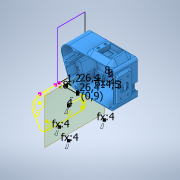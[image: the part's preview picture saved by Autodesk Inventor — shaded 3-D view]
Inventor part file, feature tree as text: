
AUTODESK INVENTOR PART (.ipt)
format: ipt  version: 2021.1 (Build 251245010, 245A)  size: 2,009,600 bytes
history: mixed  units: in
note: dims shown in document units (in); Inventor stores cm internally (conversion verified against a paired STEP export)
features: extrude x25, sketch x22, move_body x9, direct_edit x7, projected_geometry x7, chamfer x6, other x4, revolve x4, fillet x1, plane x1, imported_body x1
ambient origin geometry x8: Origin, YZ Plane, XZ Plane, XY Plane, X Axis, Y Axis, Z Axis, Center Point
bodies: Solid1 (imported_parasolid), Volumenkörper268 (imported_parasolid), Body1 (imported_parasolid)
feature tree (87):
  sketch  "Skizze1"  dims[d0=0.1575in d1=0.1575in]
  extrude  "Extrusion2"  Depth=0.1575in
  extrude  "Extrusion1"  Depth=0.1575in
  sketch  "Skizze3"  dims[d2=0.1575in d3=0.1575in]
  extrude  "Extrusion3"  Depth=0.252in TaperAngle=0.0deg
  extrude  "Extrusion4"  Depth=0.2756in TaperAngle=0.0deg
  extrude  "Extrusion5"  Depth=0.1575in
  extrude  "Extrusion6"  Depth=0.1575in
  direct_edit  "Direktbearbeitung2"
  extrude  "Extrusion8"  Depth=0.315in
  direct_edit  "Direktbearbeitung3"
  extrude  "Extrusion10"  Depth=0.1969in TaperAngle=0.0deg
  extrude  "Extrusion11"  TaperAngle=135.0deg  [1 undecoded]
  sketch  "Skizze16"  dims[d19=45.0deg d20=0.1969in d21=0.5906in d22=0.0in d23=0.0in]
  direct_edit  "Direktbearbeitung4"
  extrude  "Extrusion19"  TaperAngle=0.0deg  [1 undecoded]
  direct_edit  "Direktbearbeitung6"
  direct_edit  "Direktbearbeitung7"
  chamfer  "Fase2"  Distance=0.0157in
  extrude  "Extrusion26"  TaperAngle=135.0deg  [1 undecoded]
  chamfer  "Fase4"  Distance=0.3937in
  sketch  "Skizze29"  dims[d32=0.3937in d33=0.2362in d34=0.0in d35=0.0in d36=0.0in d37=0.0in d38=-0.0394in d39=0.0157in d40=0.0in]
  extrude  "Extrusion30"  TaperAngle=0.0deg  [1 undecoded]
  extrude  "Extrusion35"  Depth=1.0394in
  other  "Flächenverjüngung3"
  extrude  "Extrusion36"  Depth=0.0472in
  revolve  "Umdrehung1"
  sketch  "Skizze36"  dims[d45=0.3937in d46=0.0in d69=0.0in d70=0.0in d71=-0.2756in]
  fillet  "Rundung3"  Radius=0.315in
  extrude  "Extrusion37"  Depth=0.1181in TaperAngle=0.0deg
  chamfer  "Fase5"  [1 undecoded]
  plane  "Arbeitsebene2"
  extrude  "Extrusion38"  Depth=0.0197in
  extrude  "Extrusion39"  Depth=0.0197in
  extrude  "Extrusion40"  Depth=0.0197in TaperAngle=45.0deg
  chamfer  "Fase6"  Distance=0.0197in
  extrude  "Extrusion41"  Depth=0.1181in
  chamfer  "Fase7"  Distance=0.0197in
  extrude  "Extrusion42"  TaperAngle=90.0deg  [1 undecoded]
  extrude  "Extrusion9"  Depth=0.0039in TaperAngle=0.0deg
  direct_edit  "Direktbearbeitung8"
  sketch  "Skizze44"  dims[d122=0.0157in d123=0.0in d124=0.0197in d125=0.0787in d126=45.0deg d133=0.0197in d134=0.0in]
  sketch  "Skizze45"  dims[d144=0.3346in d145=0.0in d147=0.1181in]
  direct_edit  "Direktbearbeitung10"
  sketch  "Skizze47"  dims[d148=45.0deg d149=0.0197in d150=0.0in]
  extrude  "Extrusion43"  Depth=0.0039in TaperAngle=45.0deg
  extrude  "Extrusion44"  Depth=0.0039in
  chamfer  "Fase8"  Distance=0.0787in
  extrude  "Extrusion45"  Depth=0.0039in TaperAngle=0.0deg
  extrude  "Extrusion46"  Depth=0.0039in
  projected_geometry  "Projizierte Kontur2"
  sketch  "Skizze4"  dims[d4=0.1575in d5=0.252in d6=0.0in]
  sketch  "Skizze5"  dims[d7=0.2362in d8=0.0in d9=0.2756in d10=0.0in]
  sketch  "Skizze8"  dims[d11=0.1575in d12=0.0in d13=0.1575in]
  sketch  "Skizze9"  dims[d14=0.1575in d15=0.1575in]
  sketch  "Skizze10"  dims[d16=0.252in d17=0.0in d18=0.315in]
  sketch  "Skizze26"  dims[d30=0.315in d31=135.0deg]
  sketch  "Skizze35"  dims[d41=0.315in d42=135.0deg d43=0.3937in d44=0.0in]
  sketch  "Skizze37"  dims[d72=0.3937in d73=0.0in d74=1.0394in]
  projected_geometry  "Projizierte Kontur7"
  sketch  "Skizze38"  dims[d75=1.0394in d76=0.0472in d86=0.315in]
  sketch  "Skizze39"  dims[d87=0.2362in d88=0.0in d89=0.0in d90=0.1181in d104=0.0in d105=0.0in d106=-0.0787in]
  projected_geometry  "Projizierte Kontur8"
  sketch  "Skizze40"  dims[d109=0.0197in d113=0.0197in d114=0.0787in d115=45.0deg d119=0.0197in]
  projected_geometry  "Projizierte Kontur9"
  sketch  "Skizze41"  dims[d120=0.0197in d121=0.0197in]
  sketch  "Skizze48"  dims[d151=0.1969in d152=90.0deg]
  projected_geometry  "Projizierte Kontur11"
  sketch  "Skizze49"  dims[d153=0.0787in d154=0.0787in d155=0.0in d156=0.0787in d157=0.0787in d158=45.0deg d159=0.3937in d160=0.0787in d161=1.9685in d162=0.0in d163=0.1969in d164=0.1969in d165=135.0deg d166=0.0394in d167=0.0in d168=0.1575in d172=0.1811in d173=0.252in d174=0.0in d175=0.0197in d176=0.0787in d177=45.0deg d178=0.1969in d179=0.1969in d180=0.0394in d181=0.0in d182=0.0197in d183=0.0787in d184=45.0deg d185=0.0157in d186=0.0in d187=-0.6184in d188=0.0in d189=2.8346in d190=0.0in d191=4.1339in d192=0.0in d193=0.0in d194=0.0in d195=0.0in d196=1.3346in d197=-1.0433in d198=0.0in d199=0.0in d201=180.0deg d202=3.9375in d203=0.1875in d204=0.375in d205=0.1575in d206=0.315in d207=0.3937in d208=0.0in d209=0.1969in d210=0.0354in d211=0.0in d212=0.0197in d213=0.0787in d214=45.0deg d215=0.2362in d216=0.0591in d217=0.0079in d218=0.0in d219=0.5709in d220=0.0354in d221=0.0039in d222=0.0039in d223=0.3937in d224=0.0in d225=0.0687in]
  projected_geometry  "Projizierte Kontur12"
  projected_geometry  "Projizierte Kontur13"
  other  "Löschen2"
  other  "Löschen3"
  move_body  "Verschieben1"
  other  "Löschen4"
  move_body  "Verschieben2"
  move_body  "Verschieben4"
  move_body  "Verschieben5"
  revolve  "Drehen1"  [1 undecoded]
  move_body  "Verschieben6"
  move_body  "Verschieben7"
  move_body  "Verschieben8"
  move_body  "Verschieben9"
  revolve  "Drehen3"  Angle=135.0deg
  move_body  "Verschieben10"
  revolve  "Drehen4"  [1 undecoded]
  imported_body  NMx_Import_Brep_tag  [imported B-rep: ~26 faces, bbox_mm=[3.2, 9.566667, 3.3]]
note: 8 required parameter values undecoded (feature->parameter linkage not recoverable at this tier; creation-order binding heuristic only, values carry confidence <= 0.55)